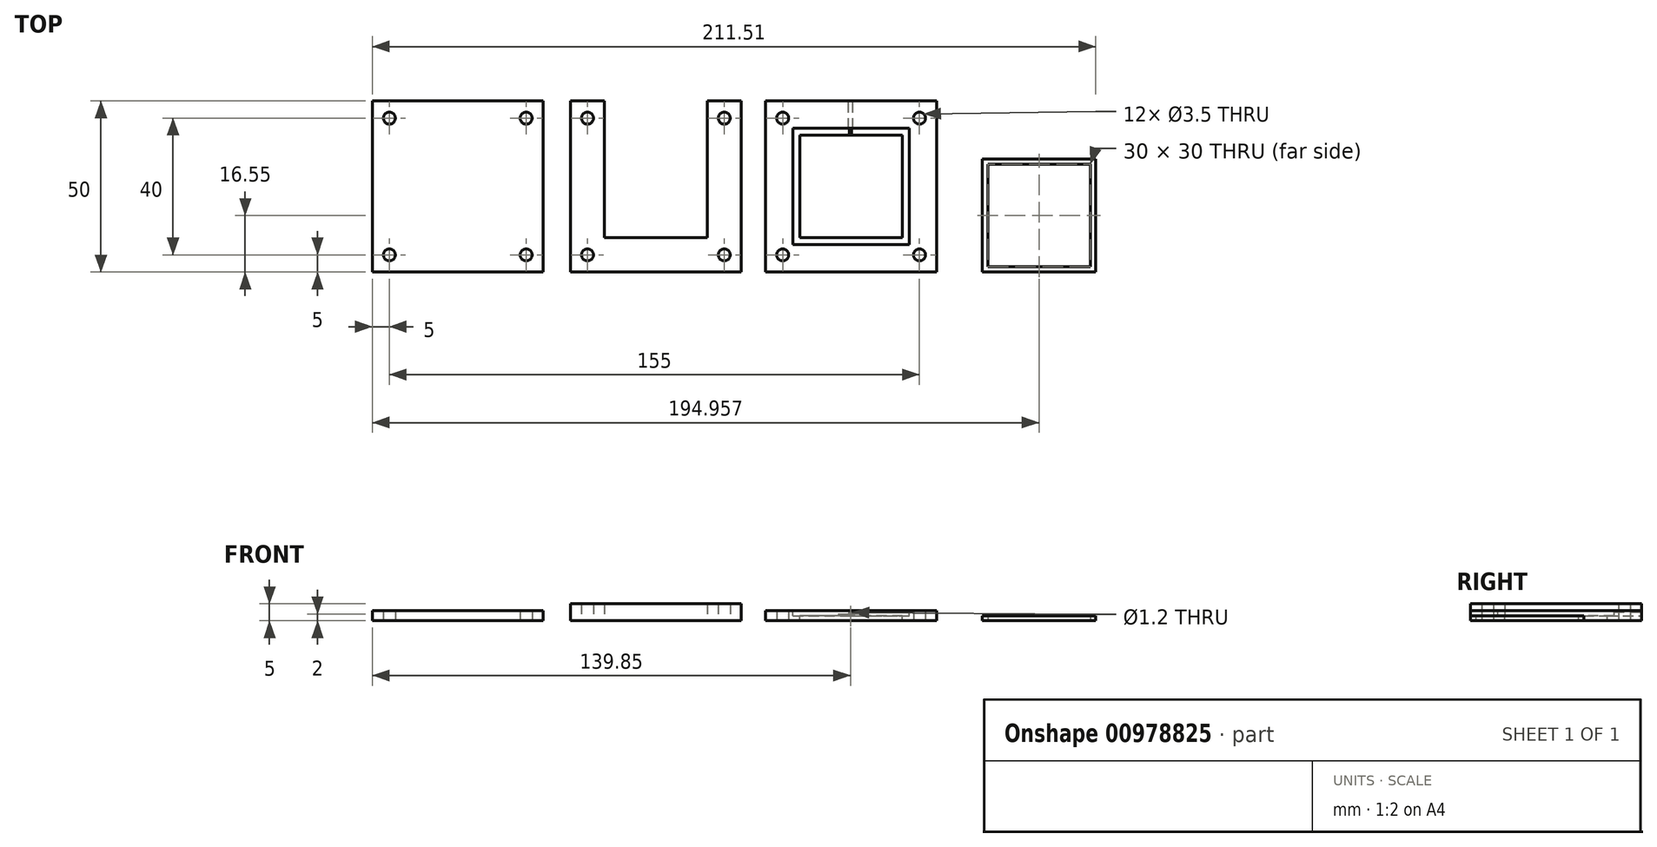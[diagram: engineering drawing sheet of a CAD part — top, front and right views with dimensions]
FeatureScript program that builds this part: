
annotation { "Feature Type Name" : "Feature", "Feature Type Description" : "" }
export const myFeature = defineFeature(function(context is Context, id is Id, definition is map)
    precondition{}
    {
        {
            var Q0;
            Q0=qCreatedBy(makeId("Top.planeOp"),FACE);
            var sketch = newSketch(context, id + "F0", { "sketchPlane" : qUnion([Q0])});
            skLineSegment(sketch, "E0.bottom", {"start": v(0, 0) * mm, "end": v(50, 0) * mm});
            skLineSegment(sketch, "E0.top", {"start": v(0, 50) * mm, "end": v(50, 50) * mm});
            skLineSegment(sketch, "E0.left", {"start": v(0, 0) * mm, "end": v(0, 50) * mm});
            skLineSegment(sketch, "E0.right", {"start": v(50, 0) * mm, "end": v(50, 50) * mm});
            skCircle(sketch, "E1", {"center": v(5, 45) * mm, "radius": 1.75 * mm});
            skCircle(sketch, "E2.0.1.0", {"center": v(5, 5) * mm, "radius": 1.75 * mm});
            skCircle(sketch, "E2.1.0.0", {"center": v(45, 45) * mm, "radius": 1.75 * mm});
            skCircle(sketch, "E2.1.1.0", {"center": v(45, 5) * mm, "radius": 1.75 * mm});
            skLineSegment(sketch, "E2.direction1", {"start": v(5, 45) * mm, "end": v(45, 45) * mm, "construction": true});
            skLineSegment(sketch, "E2.direction2", {"start": v(5, 45) * mm, "end": v(5, 5) * mm, "construction": true});
            skSolve(sketch);
        }
        {
            var Q0;
            Q0 = qSketchRegion(id + "F0", true);
            extrude(context, id + "F1", {"entities" : qUnion([Q0]), "depth" : 3 * mm, "offsetDistance" : 25 * mm});
        }
        {
            var Q0;
            Q0=qCreatedBy(makeId("Top.planeOp"),FACE);
            var sketch = newSketch(context, id + "F2", { "sketchPlane" : qUnion([Q0])});
            skLineSegment(sketch, "E3.bottom", {"start": v(57.92, 50) * mm, "end": v(67.92, 50) * mm});
            skLineSegment(sketch, "E3.top", {"start": v(57.92, 0) * mm, "end": v(67.92, 0) * mm});
            skLineSegment(sketch, "E3.left", {"start": v(57.92, 50) * mm, "end": v(57.92, 0) * mm});
            skLineSegment(sketch, "E3.right", {"start": v(67.92, 50) * mm, "end": v(67.92, 0) * mm});
            skLineSegment(sketch, "E4.bottom", {"start": v(67.92, 0) * mm, "end": v(97.92, 0) * mm});
            skLineSegment(sketch, "E4.top", {"start": v(67.92, 10) * mm, "end": v(97.92, 10) * mm});
            skLineSegment(sketch, "E4.left", {"start": v(67.92, 0) * mm, "end": v(67.92, 10) * mm});
            skLineSegment(sketch, "E4.right", {"start": v(97.92, 0) * mm, "end": v(97.92, 10) * mm});
            skLineSegment(sketch, "E5.bottom", {"start": v(97.92, 0) * mm, "end": v(107.92, 0) * mm});
            skLineSegment(sketch, "E5.top", {"start": v(97.92, 50) * mm, "end": v(107.92, 50) * mm});
            skLineSegment(sketch, "E5.left", {"start": v(97.92, 0) * mm, "end": v(97.92, 50) * mm});
            skLineSegment(sketch, "E5.right", {"start": v(107.92, 0) * mm, "end": v(107.92, 50) * mm});
            skCircle(sketch, "E6", {"center": v(62.92, 45) * mm, "radius": 1.75 * mm});
            skCircle(sketch, "E7.0.1.0", {"center": v(62.92, 5) * mm, "radius": 1.75 * mm});
            skCircle(sketch, "E7.1.0.0", {"center": v(102.92, 45) * mm, "radius": 1.75 * mm});
            skCircle(sketch, "E7.1.1.0", {"center": v(102.92, 5) * mm, "radius": 1.75 * mm});
            skLineSegment(sketch, "E7.direction1", {"start": v(62.92, 45) * mm, "end": v(102.92, 45) * mm, "construction": true});
            skLineSegment(sketch, "E7.direction2", {"start": v(62.92, 45) * mm, "end": v(62.92, 5) * mm, "construction": true});
            skSolve(sketch);
        }
        {
            var Q0;
            Q0 = qSketchRegion(id + "F2", true);
            extrude(context, id + "F3", {"entities" : qUnion([Q0]), "depth" : 5 * mm, "offsetDistance" : 25 * mm});
        }
        {
            var Q0;
            Q0=makeQuery(id+"F1.opExtrude","SWEPT_BODY",BODY,{"disambiguationData":[OSD([sQuery(id+"F0.wireOp",EDGE,"E0.bottom"),sQuery(id+"F0.wireOp",EDGE,"E0.top"),sQuery(id+"F0.wireOp",EDGE,"E0.left"),sQuery(id+"F0.wireOp",EDGE,"E0.right"),sQuery(id+"F0.wireOp",EDGE,"E1"),sQuery(id+"F0.wireOp",EDGE,"E2.0.1.0"),sQuery(id+"F0.wireOp",EDGE,"E2.1.0.0"),sQuery(id+"F0.wireOp",EDGE,"E2.1.1.0")])]});
            transform(context, id + "F4", {"entities" : qUnion([Q0]), "transformType" : TransformType.TRANSLATION_3D, "dx" : 115 * mm, "dy" : 0 * mm, "dz" : 0 * mm, "makeCopy" : true});
        }
        {
            var Q0;
            Q0=makeQuery(id+"F4.opPattern","COPY",FACE,{"derivedFrom":makeQuery(id+"F1.opExtrude","CAP_FACE",FACE,{"disambiguationData":[OSD([sQuery(id+"F0.wireOp",EDGE,"E0.bottom"),sQuery(id+"F0.wireOp",EDGE,"E0.top"),sQuery(id+"F0.wireOp",EDGE,"E0.left"),sQuery(id+"F0.wireOp",EDGE,"E0.right"),sQuery(id+"F0.wireOp",EDGE,"E1"),sQuery(id+"F0.wireOp",EDGE,"E2.0.1.0"),sQuery(id+"F0.wireOp",EDGE,"E2.1.0.0"),sQuery(id+"F0.wireOp",EDGE,"E2.1.1.0")])],"isStart":false}),"instanceName":"1"});
            var sketch = newSketch(context, id + "F5", { "sketchPlane" : qUnion([Q0])});
            skLineSegment(sketch, "E8.bottom", {"start": v(125, 40) * mm, "end": v(155, 40) * mm});
            skLineSegment(sketch, "E8.top", {"start": v(125, 10) * mm, "end": v(155, 10) * mm});
            skLineSegment(sketch, "E8.left", {"start": v(125, 40) * mm, "end": v(125, 10) * mm});
            skLineSegment(sketch, "E8.right", {"start": v(155, 40) * mm, "end": v(155, 10) * mm});
            skSolve(sketch);
        }
        {
            var Q0;
            Q0 = qSketchRegion(id + "F5", true);
            extrude(context, id + "F6", {"entities" : qUnion([Q0]), "operationType" : NewBodyOperationType.REMOVE, "endBound" : BoundingType.THROUGH_ALL, "oppositeDirection" : true, "depth" : 25 * mm, "offsetDistance" : 25 * mm});
        }
        {
            var Q0;
            Q0=makeQuery(id+"F4.opPattern","COPY",FACE,{"derivedFrom":makeQuery(id+"F1.opExtrude","CAP_FACE",FACE,{"disambiguationData":[OSD([sQuery(id+"F0.wireOp",EDGE,"E0.bottom"),sQuery(id+"F0.wireOp",EDGE,"E0.top"),sQuery(id+"F0.wireOp",EDGE,"E0.left"),sQuery(id+"F0.wireOp",EDGE,"E0.right"),sQuery(id+"F0.wireOp",EDGE,"E1"),sQuery(id+"F0.wireOp",EDGE,"E2.0.1.0"),sQuery(id+"F0.wireOp",EDGE,"E2.1.0.0"),sQuery(id+"F0.wireOp",EDGE,"E2.1.1.0")])],"isStart":false}),"instanceName":"1"});
            var sketch = newSketch(context, id + "F7", { "sketchPlane" : qUnion([Q0])});
            skLineSegment(sketch, "E9.bottom", {"start": v(123, 42) * mm, "end": v(157, 42) * mm});
            skLineSegment(sketch, "E9.top", {"start": v(123, 8) * mm, "end": v(157, 8) * mm});
            skLineSegment(sketch, "E9.left", {"start": v(123, 42) * mm, "end": v(123, 8) * mm});
            skLineSegment(sketch, "E9.right", {"start": v(157, 42) * mm, "end": v(157, 8) * mm});
            skSolve(sketch);
        }
        {
            var Q0;
            Q0 = qSketchRegion(id + "F7", true);
            extrude(context, id + "F8", {"entities" : qUnion([Q0]), "operationType" : NewBodyOperationType.REMOVE, "oppositeDirection" : true, "depth" : 1.5 * mm, "offsetDistance" : 25 * mm});
        }
        {
            var Q0;
            Q0=qCreatedBy(makeId("Top.planeOp"),FACE);
            var sketch = newSketch(context, id + "F9", { "sketchPlane" : qUnion([Q0])});
            skLineSegment(sketch, "E10.bottom", {"start": v(178.4, 0) * mm, "end": v(211.5, 0) * mm});
            skLineSegment(sketch, "E10.top", {"start": v(178.4, 33.1) * mm, "end": v(211.5, 33.1) * mm});
            skLineSegment(sketch, "E10.left", {"start": v(178.4, 0) * mm, "end": v(178.4, 33.1) * mm});
            skLineSegment(sketch, "E10.right", {"start": v(211.5, 0) * mm, "end": v(211.5, 33.1) * mm});
            skLineSegment(sketch, "E11.bottom", {"start": v(179.96, 1.55) * mm, "end": v(209.96, 1.55) * mm});
            skLineSegment(sketch, "E11.top", {"start": v(179.96, 31.55) * mm, "end": v(209.96, 31.55) * mm});
            skLineSegment(sketch, "E11.left", {"start": v(179.96, 1.55) * mm, "end": v(179.96, 31.55) * mm});
            skLineSegment(sketch, "E11.right", {"start": v(209.96, 1.55) * mm, "end": v(209.96, 31.55) * mm});
            skSolve(sketch);
        }
        {
            var Q0;
            Q0 = qSketchRegion(id + "F9", true);
            extrude(context, id + "F10", {"entities" : qUnion([Q0]), "depth" : 1.4 * mm, "offsetDistance" : 25 * mm});
        }
        {
            var Q0;
            Q0=makeQuery(id+"F4.opPattern","COPY",FACE,{"derivedFrom":makeQuery(id+"F1.opExtrude","SWEPT_FACE",FACE,{"disambiguationData":[OSD([sQuery(id+"F0.wireOp",EDGE,"E0.top")])]}),"instanceName":"1"});
            var sketch = newSketch(context, id + "F11", { "sketchPlane" : qUnion([Q0])});
            skCircle(sketch, "E12", {"center": v(-139.85, 2) * mm, "radius": 0.6 * mm});
            skSolve(sketch);
        }
        {
            var Q0;
            Q0 = qSketchRegion(id + "F11", true);
            extrude(context, id + "F12", {"entities" : qUnion([Q0]), "operationType" : NewBodyOperationType.REMOVE, "oppositeDirection" : true, "depth" : 25 * mm, "offsetDistance" : 25 * mm});
        }
    });
